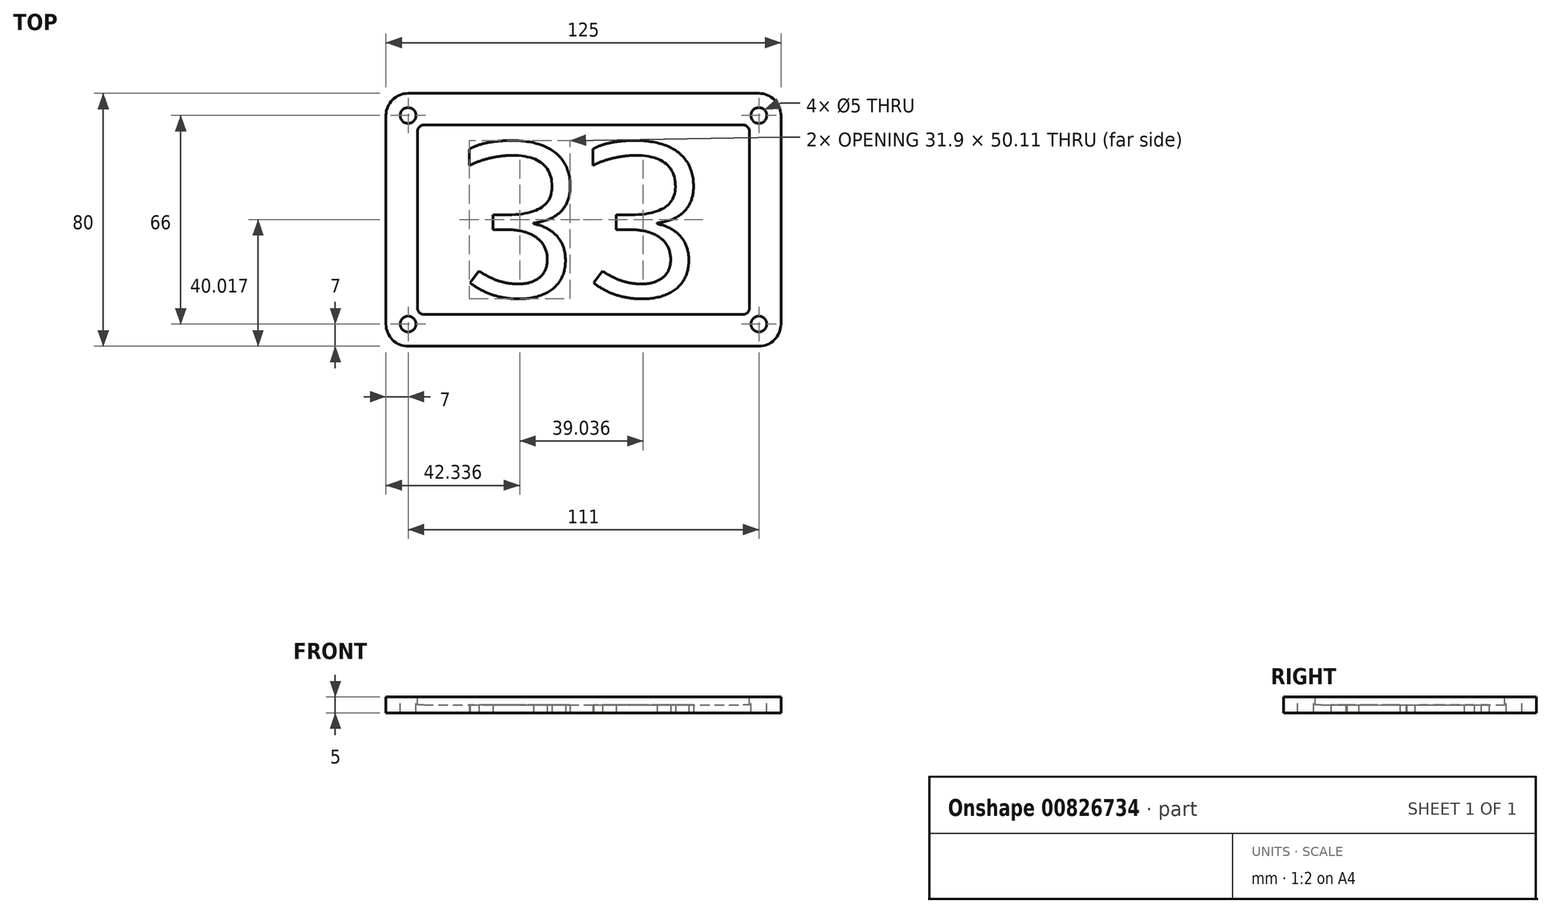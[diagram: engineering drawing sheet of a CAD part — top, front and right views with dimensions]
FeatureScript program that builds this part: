
annotation { "Feature Type Name" : "Feature", "Feature Type Description" : "" }
export const myFeature = defineFeature(function(context is Context, id is Id, definition is map)
    precondition{}
    {
        {
            var Q0;
            Q0=qCreatedBy(makeId("Top.planeOp"),FACE);
            var sketch = newSketch(context, id + "F0", { "sketchPlane" : qUnion([Q0])});
            skLineSegment(sketch, "E0.bottom", {"start": v(55.5, -40) * mm, "end": v(-55.5, -40) * mm});
            skLineSegment(sketch, "E0.top", {"start": v(55.5, 40) * mm, "end": v(-55.5, 40) * mm});
            skLineSegment(sketch, "E0.left", {"start": v(62.5, -33) * mm, "end": v(62.5, 33) * mm});
            skLineSegment(sketch, "E0.right", {"start": v(-62.5, -33) * mm, "end": v(-62.5, 33) * mm});
            skPoint(sketch, "E0.middle", {"position": v(0, 0) * mm});
            skPoint(sketch, "E1.visualSharp", {"position": v(-62.5, 40) * mm});
            skArc(sketch, "E1.filletArc", {"start": v(-55.5, 40) * mm, "mid": v(-60.45, 37.95) * mm, "end": v(-62.5, 33) * mm});
            skPoint(sketch, "E2.visualSharp", {"position": v(62.5, 40) * mm});
            skArc(sketch, "E2.filletArc", {"start": v(62.5, 33) * mm, "mid": v(60.45, 37.95) * mm, "end": v(55.5, 40) * mm});
            skPoint(sketch, "E3.visualSharp", {"position": v(62.5, -40) * mm});
            skArc(sketch, "E3.filletArc", {"start": v(55.5, -40) * mm, "mid": v(60.45, -37.95) * mm, "end": v(62.5, -33) * mm});
            skPoint(sketch, "E4.visualSharp", {"position": v(-62.5, -40) * mm});
            skArc(sketch, "E4.filletArc", {"start": v(-62.5, -33) * mm, "mid": v(-60.45, -37.95) * mm, "end": v(-55.5, -40) * mm});
            skSolve(sketch);
        }
        {
            var Q0;
            Q0=makeQuery(id+"F0.imprint","IMPRINT",FACE,{"disambiguationData":[TD([[makeQuery(id+"F0.imprint","IMPRINT",EDGE,{"derivedFrom":sQuery(id+"F0.wireOp",EDGE,"E0.bottom")}),-1.0]])]});
            extrude(context, id + "F1", {"entities" : qUnion([Q0]), "depth" : 5 * mm, "offsetDistance" : 25 * mm});
        }
        {
            var Q0;
            Q0=makeQuery(id+"F1.opExtrude","CAP_FACE",FACE,{"disambiguationData":[OSD([sQuery(id+"F0.wireOp",EDGE,"E0.bottom"),sQuery(id+"F0.wireOp",EDGE,"E0.top"),sQuery(id+"F0.wireOp",EDGE,"E0.left"),sQuery(id+"F0.wireOp",EDGE,"E0.right"),sQuery(id+"F0.wireOp",EDGE,"E1.filletArc"),sQuery(id+"F0.wireOp",EDGE,"E2.filletArc"),sQuery(id+"F0.wireOp",EDGE,"E3.filletArc"),sQuery(id+"F0.wireOp",EDGE,"E4.filletArc")])],"isStart":false});
            var sketch = newSketch(context, id + "F2", { "sketchPlane" : qUnion([Q0])});
            skLineSegment(sketch, "E5.bottom", {"start": v(-50.5, -30) * mm, "end": v(50.5, -30) * mm});
            skLineSegment(sketch, "E5.top", {"start": v(-50.5, 30) * mm, "end": v(50.5, 30) * mm});
            skLineSegment(sketch, "E5.left", {"start": v(-52.5, -28) * mm, "end": v(-52.5, 28) * mm});
            skLineSegment(sketch, "E5.right", {"start": v(52.5, -28) * mm, "end": v(52.5, 28) * mm});
            skPoint(sketch, "E5.middle", {"position": v(0, 0) * mm});
            skPoint(sketch, "E6.visualSharp", {"position": v(-52.5, 30) * mm});
            skArc(sketch, "E6.filletArc", {"start": v(-50.5, 30) * mm, "mid": v(-51.91, 29.41) * mm, "end": v(-52.5, 28) * mm});
            skPoint(sketch, "E7.visualSharp", {"position": v(52.5, 30) * mm});
            skArc(sketch, "E7.filletArc", {"start": v(52.5, 28) * mm, "mid": v(51.91, 29.41) * mm, "end": v(50.5, 30) * mm});
            skPoint(sketch, "E8.visualSharp", {"position": v(52.5, -30) * mm});
            skArc(sketch, "E8.filletArc", {"start": v(50.5, -30) * mm, "mid": v(51.91, -29.41) * mm, "end": v(52.5, -28) * mm});
            skPoint(sketch, "E9.visualSharp", {"position": v(-52.5, -30) * mm});
            skArc(sketch, "E9.filletArc", {"start": v(-52.5, -28) * mm, "mid": v(-51.91, -29.41) * mm, "end": v(-50.5, -30) * mm});
            skSolve(sketch);
        }
        {
            var Q0;
            Q0=makeQuery(id+"F2.imprint","IMPRINT",FACE,{"disambiguationData":[TD([[makeQuery(id+"F2.imprint","IMPRINT",EDGE,{"derivedFrom":sQuery(id+"F2.wireOp",EDGE,"E5.bottom")}),1.0]])]});
            extrude(context, id + "F3", {"entities" : qUnion([Q0]), "operationType" : NewBodyOperationType.REMOVE, "oppositeDirection" : true, "depth" : 2.5 * mm, "offsetDistance" : 25 * mm});
        }
        {
            var Q0;
            Q0=makeQuery(id+"F1.opExtrude","CAP_FACE",FACE,{"disambiguationData":[OSD([sQuery(id+"F0.wireOp",EDGE,"E0.bottom"),sQuery(id+"F0.wireOp",EDGE,"E0.top"),sQuery(id+"F0.wireOp",EDGE,"E0.left"),sQuery(id+"F0.wireOp",EDGE,"E0.right"),sQuery(id+"F0.wireOp",EDGE,"E1.filletArc"),sQuery(id+"F0.wireOp",EDGE,"E2.filletArc"),sQuery(id+"F0.wireOp",EDGE,"E3.filletArc"),sQuery(id+"F0.wireOp",EDGE,"E4.filletArc")])],"isStart":false});
            var sketch = newSketch(context, id + "F4", { "sketchPlane" : qUnion([Q0])});
            skCircle(sketch, "E10", {"center": v(-55.5, 33) * mm, "radius": 2.5 * mm});
            skCircle(sketch, "E11", {"center": v(55.5, 33) * mm, "radius": 2.5 * mm});
            skCircle(sketch, "E12", {"center": v(-55.5, -33) * mm, "radius": 2.5 * mm});
            skCircle(sketch, "E13", {"center": v(55.5, -33) * mm, "radius": 2.5 * mm});
            skSolve(sketch);
        }
        {
            var Q0;
            Q0=makeQuery(id+"F4.imprint","IMPRINT",FACE,{"disambiguationData":[TD([[makeQuery(id+"F4.imprint","IMPRINT",EDGE,{"derivedFrom":sQuery(id+"F4.wireOp",EDGE,"E12")}),1.0]])]});
            var Q1;
            Q1=makeQuery(id+"F4.imprint","IMPRINT",FACE,{"disambiguationData":[TD([[makeQuery(id+"F4.imprint","IMPRINT",EDGE,{"derivedFrom":sQuery(id+"F4.wireOp",EDGE,"E10")}),1.0]])]});
            var Q2;
            Q2=makeQuery(id+"F4.imprint","IMPRINT",FACE,{"disambiguationData":[TD([[makeQuery(id+"F4.imprint","IMPRINT",EDGE,{"derivedFrom":sQuery(id+"F4.wireOp",EDGE,"E11")}),1.0]])]});
            var Q3;
            Q3=makeQuery(id+"F4.imprint","IMPRINT",FACE,{"disambiguationData":[TD([[makeQuery(id+"F4.imprint","IMPRINT",EDGE,{"derivedFrom":sQuery(id+"F4.wireOp",EDGE,"E13")}),1.0]])]});
            extrude(context, id + "F5", {"entities" : qUnion([Q0, Q1, Q2, Q3]), "operationType" : NewBodyOperationType.REMOVE, "endBound" : BoundingType.THROUGH_ALL, "oppositeDirection" : true, "depth" : 5 * mm, "offsetDistance" : 25 * mm});
        }
        {
            var Q0;
            Q0=makeQuery(id+"F1.opExtrude","CAP_FACE",FACE,{"disambiguationData":[OSD([sQuery(id+"F0.wireOp",EDGE,"E0.bottom"),sQuery(id+"F0.wireOp",EDGE,"E0.top"),sQuery(id+"F0.wireOp",EDGE,"E0.left"),sQuery(id+"F0.wireOp",EDGE,"E0.right"),sQuery(id+"F0.wireOp",EDGE,"E1.filletArc"),sQuery(id+"F0.wireOp",EDGE,"E2.filletArc"),sQuery(id+"F0.wireOp",EDGE,"E3.filletArc"),sQuery(id+"F0.wireOp",EDGE,"E4.filletArc")])],"isStart":true});
            var sketch = newSketch(context, id + "F6", { "sketchPlane" : qUnion([Q0])});
            skText(sketch, "E14", { "text": "33", "fontName": "OpenSans-Regular.ttf"});
            const initialGuessF6  = {"E14": [-0.03925, -0.0244, 1, 0, 0.04916]};
            skSetInitialGuess(sketch, initialGuessF6);
            skSolve(sketch);
        }
        {
            var Q0;
            Q0=makeQuery(id+"F6.imprint","IMPRINT",FACE,{"disambiguationData":[TD([[makeQuery(id+"F6.imprint","IMPRINT",EDGE,{"derivedFrom":sQuery(id+"F6.wireOp",EDGE,"E14.sketch_text.stroke-0")}),-1.0]])]});
            var Q1;
            Q1=makeQuery(id+"F6.imprint","IMPRINT",FACE,{"disambiguationData":[TD([[makeQuery(id+"F6.imprint","IMPRINT",EDGE,{"derivedFrom":sQuery(id+"F6.wireOp",EDGE,"E14.sketch_text.stroke-28")}),-1.0]])]});
            extrude(context, id + "F7", {"entities" : qUnion([Q0, Q1]), "operationType" : NewBodyOperationType.REMOVE, "endBound" : BoundingType.THROUGH_ALL, "oppositeDirection" : true, "depth" : 25 * mm, "offsetDistance" : 25 * mm});
        }
    });
